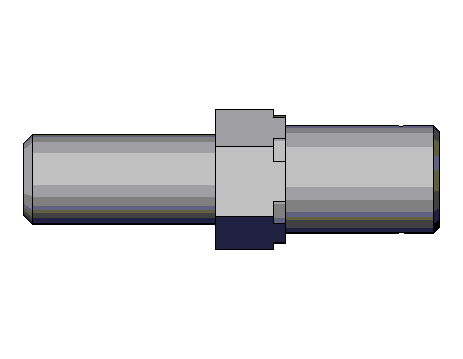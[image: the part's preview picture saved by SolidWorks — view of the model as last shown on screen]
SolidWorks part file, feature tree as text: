
SOLIDWORKS PART (.sldprt)
format: sldprt  version: not decoded by parser v0  size: 187,904 bytes
history: native  units: mm
features: sketch x4, extrude x4, plane x3, material x1, cut_revolve x1, chamfer x1, cut_extrude x1 (+8 scaffold rows collapsed)
feature tree (23):
  scaffold x8  (default folders/planes/origin — collapsed)
  material  "Matériau <non spécifié>"
  plane  "Face"
  plane  "Dessus"
  plane  "Droite"
  sketch  "Esquisse1"  dims[D1=19.0mm]
  extrude  "Extrusion1"  Depth=31mm
  sketch  "Esquisse2"  dims[c1.D1=11.0mm c1.D2=10.0mm c1.D3=8.5mm c2.D1=7.45mm c2.D4=~3.086029mm c2.D5=1.0mm]
  cut_revolve  "Enlèvement de matière-Révolution1"  Angle=360deg
  chamfer  "Chanfrein1"  Distance=1mm Angle=45deg
  sketch  "Esquisse4"  dims[D1=14.0mm]
  extrude  "Extrusion2"  Depth=30mm
  extrude  "Chanfrein3"  Depth=1.5mm
  sketch  "Esquisse5"  dims[D2=2.75mm D1=18.0mm]
  cut_extrude  "Enlèv. mat.-Extru.1"  [1 undecoded]
  extrude  "Chanfrein4"  Depth=0.25mm
decode coverage: 10 of 11 modeling features carry decoded parameters
note: ~ marks probable driven/reference dimensions
note: 1 parameter value undecoded
note: suppression state not decoded; provenance and decode notes live in map.json
